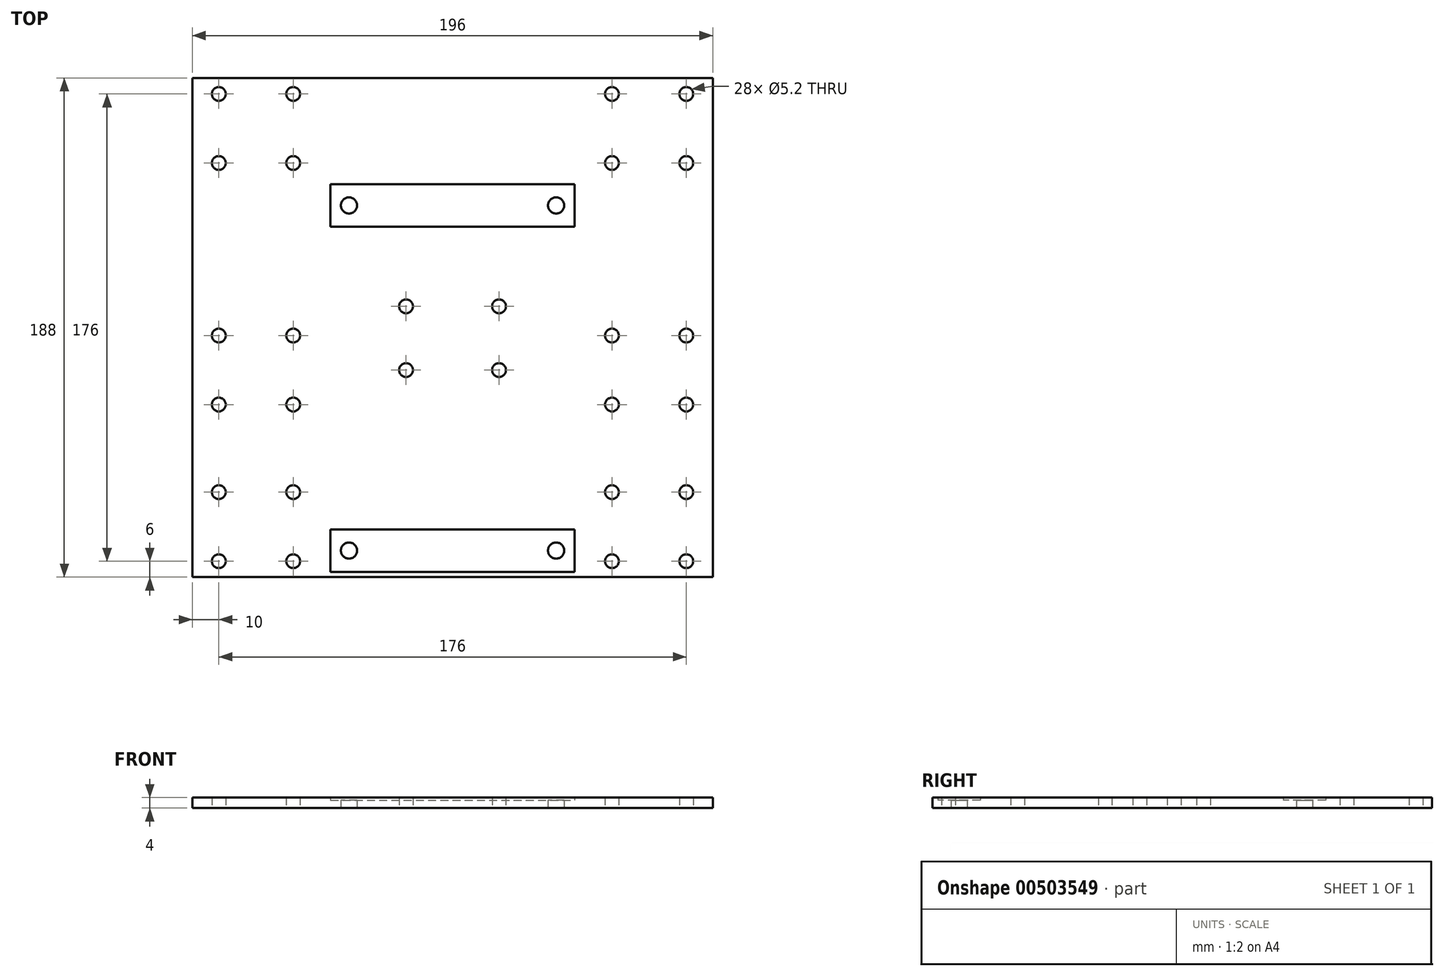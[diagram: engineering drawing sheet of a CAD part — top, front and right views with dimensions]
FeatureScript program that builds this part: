
annotation { "Feature Type Name" : "Feature", "Feature Type Description" : "" }
export const myFeature = defineFeature(function(context is Context, id is Id, definition is map)
    precondition{}
    {
        {
            var Q0;
            Q0=qCreatedBy(makeId("Top.planeOp"),FACE);
            var sketch = newSketch(context, id + "F0", { "sketchPlane" : qUnion([Q0])});
            skLineSegment(sketch, "E0.bottom", {"start": v(0, 0) * mm, "end": v(196, 0) * mm});
            skLineSegment(sketch, "E0.top", {"start": v(0, 188) * mm, "end": v(196, 188) * mm});
            skLineSegment(sketch, "E0.left", {"start": v(0, 0) * mm, "end": v(0, 188) * mm});
            skLineSegment(sketch, "E0.right", {"start": v(196, 0) * mm, "end": v(196, 188) * mm});
            skCircle(sketch, "E1", {"center": v(59, 10) * mm, "radius": 3.05 * mm});
            skCircle(sketch, "E2", {"center": v(59, 140) * mm, "radius": 3.05 * mm});
            skCircle(sketch, "E3", {"center": v(137, 140) * mm, "radius": 3.05 * mm});
            skCircle(sketch, "E4", {"center": v(137, 10) * mm, "radius": 3.05 * mm});
            skCircle(sketch, "E5", {"center": v(10, 182) * mm, "radius": 2.6 * mm});
            skCircle(sketch, "E6", {"center": v(38, 182) * mm, "radius": 2.6 * mm});
            skCircle(sketch, "E7", {"center": v(10, 156) * mm, "radius": 2.6 * mm});
            skCircle(sketch, "E8", {"center": v(38, 156) * mm, "radius": 2.6 * mm});
            skCircle(sketch, "E9", {"center": v(10, 91) * mm, "radius": 2.6 * mm});
            skCircle(sketch, "E10", {"center": v(38, 91) * mm, "radius": 2.6 * mm});
            skCircle(sketch, "E11", {"center": v(10, 65) * mm, "radius": 2.6 * mm});
            skCircle(sketch, "E12", {"center": v(38, 65) * mm, "radius": 2.6 * mm});
            skCircle(sketch, "E13", {"center": v(158, 182) * mm, "radius": 2.6 * mm});
            skCircle(sketch, "E14", {"center": v(186, 182) * mm, "radius": 2.6 * mm});
            skCircle(sketch, "E15", {"center": v(158, 156) * mm, "radius": 2.6 * mm});
            skCircle(sketch, "E16", {"center": v(186, 156) * mm, "radius": 2.6 * mm});
            skCircle(sketch, "E17", {"center": v(158, 91) * mm, "radius": 2.6 * mm});
            skCircle(sketch, "E18", {"center": v(186, 91) * mm, "radius": 2.6 * mm});
            skCircle(sketch, "E19", {"center": v(158, 65) * mm, "radius": 2.6 * mm});
            skCircle(sketch, "E20", {"center": v(186, 65) * mm, "radius": 2.6 * mm});
            skCircle(sketch, "E21", {"center": v(80.5, 102) * mm, "radius": 2.6 * mm});
            skCircle(sketch, "E22", {"center": v(115.5, 102) * mm, "radius": 2.6 * mm});
            skLineSegment(sketch, "E23.bottom", {"start": v(52, 148) * mm, "end": v(144, 148) * mm});
            skLineSegment(sketch, "E23.top", {"start": v(52, 132) * mm, "end": v(144, 132) * mm});
            skLineSegment(sketch, "E23.left", {"start": v(52, 148) * mm, "end": v(52, 132) * mm});
            skLineSegment(sketch, "E23.right", {"start": v(144, 148) * mm, "end": v(144, 132) * mm});
            skLineSegment(sketch, "E24.bottom", {"start": v(52, 18) * mm, "end": v(144, 18) * mm});
            skLineSegment(sketch, "E24.top", {"start": v(52, 2) * mm, "end": v(144, 2) * mm});
            skLineSegment(sketch, "E24.left", {"start": v(52, 18) * mm, "end": v(52, 2) * mm});
            skLineSegment(sketch, "E24.right", {"start": v(144, 18) * mm, "end": v(144, 2) * mm});
            skCircle(sketch, "E25", {"center": v(80.5, 78) * mm, "radius": 2.6 * mm});
            skCircle(sketch, "E26", {"center": v(115.5, 78) * mm, "radius": 2.6 * mm});
            skCircle(sketch, "E27", {"center": v(158, 32) * mm, "radius": 2.6 * mm});
            skCircle(sketch, "E28", {"center": v(186, 32) * mm, "radius": 2.6 * mm});
            skCircle(sketch, "E29", {"center": v(158, 6) * mm, "radius": 2.6 * mm});
            skCircle(sketch, "E30", {"center": v(186, 6) * mm, "radius": 2.6 * mm});
            skCircle(sketch, "E31", {"center": v(10, 32) * mm, "radius": 2.6 * mm});
            skCircle(sketch, "E32", {"center": v(38, 32) * mm, "radius": 2.6 * mm});
            skCircle(sketch, "E33", {"center": v(10, 6) * mm, "radius": 2.6 * mm});
            skCircle(sketch, "E34", {"center": v(38, 6) * mm, "radius": 2.6 * mm});
            skSolve(sketch);
        }
        {
            var Q0;
            Q0=makeQuery(id+"F0.imprint","IMPRINT",FACE,{"disambiguationData":[TD([[makeQuery(id+"F0.imprint","IMPRINT",EDGE,{"derivedFrom":sQuery(id+"F0.wireOp",EDGE,"E0.bottom")}),1.0]])]});
            extrude(context, id + "F1", {"entities" : qUnion([Q0]), "depth" : 4 * mm});
        }
        {
            var Q0;
            Q0=makeQuery(id+"F0.imprint","IMPRINT",FACE,{"disambiguationData":[TD([[makeQuery(id+"F0.imprint","IMPRINT",EDGE,{"derivedFrom":sQuery(id+"F0.wireOp",EDGE,"E2")}),-1.0]])]});
            var Q1;
            Q1=makeQuery(id+"F0.imprint","IMPRINT",FACE,{"disambiguationData":[TD([[makeQuery(id+"F0.imprint","IMPRINT",EDGE,{"derivedFrom":sQuery(id+"F0.wireOp",EDGE,"E1")}),-1.0]])]});
            extrude(context, id + "F2", {"entities" : qUnion([Q0, Q1]), "operationType" : NewBodyOperationType.ADD, "depth" : 3 * mm, "offsetDistance" : 25 * mm});
        }
    });
